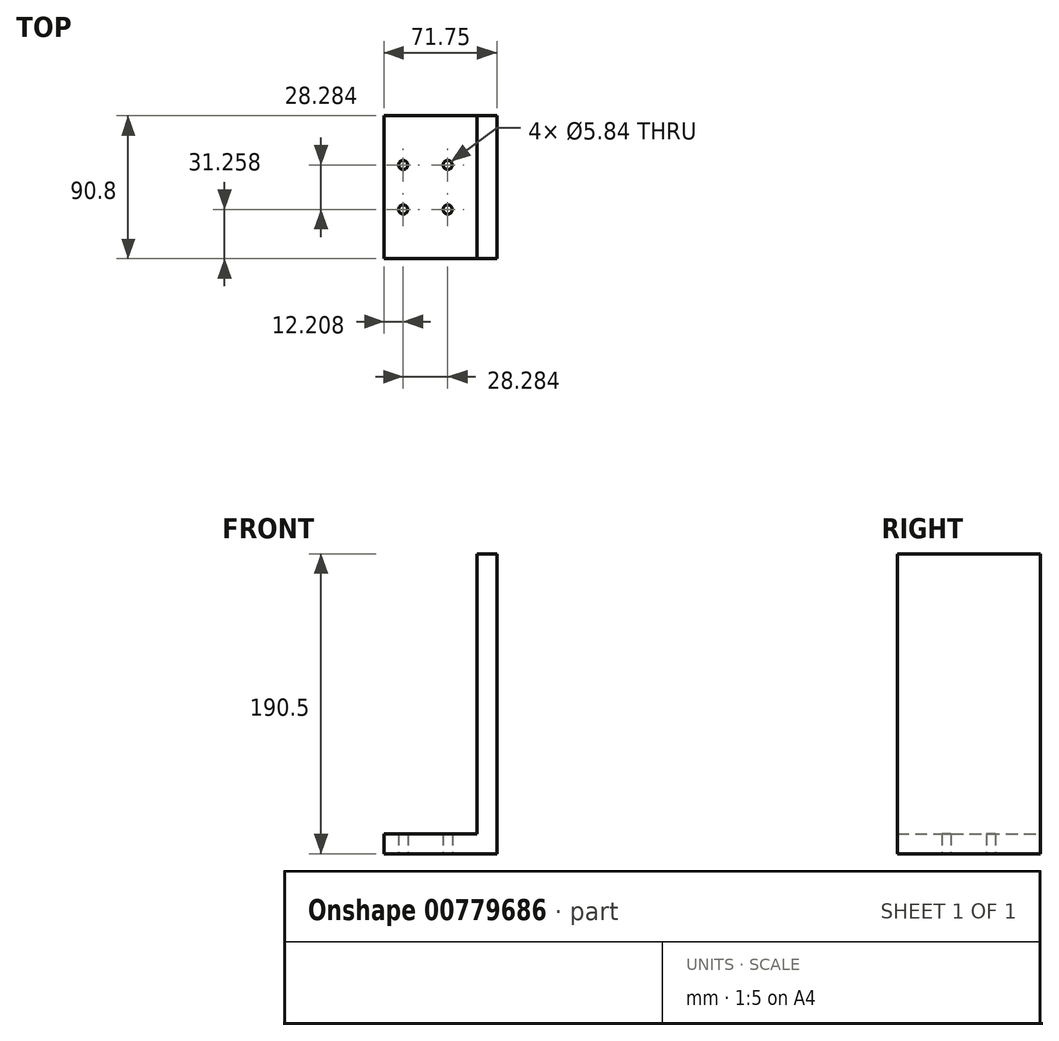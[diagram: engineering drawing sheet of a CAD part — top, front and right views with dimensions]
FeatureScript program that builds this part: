
annotation { "Feature Type Name" : "Feature", "Feature Type Description" : "" }
export const myFeature = defineFeature(function(context is Context, id is Id, definition is map)
    precondition{}
    {
        {
            var Q0;
            Q0=qCreatedBy(makeId("Top.planeOp"),FACE);
            var sketch = newSketch(context, id + "F0", { "sketchPlane" : qUnion([Q0])});
            skCircle(sketch, "E0", {"center": v(0, 0) * mm, "radius": 20 * mm, "construction": true});
            skLineSegment(sketch, "E1.bottom", {"start": v(20, 20) * mm, "end": v(-20, 20) * mm, "construction": true});
            skLineSegment(sketch, "E1.top", {"start": v(20, -20) * mm, "end": v(-20, -20) * mm, "construction": true});
            skLineSegment(sketch, "E1.left", {"start": v(20, 20) * mm, "end": v(20, -20) * mm, "construction": true});
            skLineSegment(sketch, "E1.right", {"start": v(-20, 20) * mm, "end": v(-20, -20) * mm, "construction": true});
            skLineSegment(sketch, "E2", {"start": v(-20, 20) * mm, "end": v(20, -20) * mm, "construction": true});
            skLineSegment(sketch, "E3", {"start": v(-20, -20) * mm, "end": v(20, 20) * mm, "construction": true});
            skCircle(sketch, "E4", {"center": v(-14.14, 14.14) * mm, "radius": 2.92 * mm});
            skCircle(sketch, "E5", {"center": v(14.14, 14.14) * mm, "radius": 2.92 * mm});
            skCircle(sketch, "E6", {"center": v(14.14, -14.14) * mm, "radius": 2.92 * mm});
            skCircle(sketch, "E7", {"center": v(-14.14, -14.14) * mm, "radius": 2.92 * mm});
            skLineSegment(sketch, "E8.bottom", {"start": v(-26.35, 45.4) * mm, "end": v(45.4, 45.4) * mm});
            skLineSegment(sketch, "E8.top", {"start": v(-26.35, -45.4) * mm, "end": v(45.4, -45.4) * mm});
            skLineSegment(sketch, "E8.left", {"start": v(-26.35, 45.4) * mm, "end": v(-26.35, -45.4) * mm});
            skLineSegment(sketch, "E8.right", {"start": v(45.4, 45.4) * mm, "end": v(45.4, -45.4) * mm});
            skLineSegment(sketch, "E9.bottom", {"start": v(45.4, 45.4) * mm, "end": v(32.7, 45.4) * mm});
            skLineSegment(sketch, "E9.top", {"start": v(45.4, -45.4) * mm, "end": v(32.7, -45.4) * mm});
            skLineSegment(sketch, "E9.right", {"start": v(32.7, 45.4) * mm, "end": v(32.7, -45.4) * mm});
            skSolve(sketch);
        }
        {
            var Q0;
            {var subQ0=sQuery(id+"F0.wireOp",EDGE,"E8.right");Q0=makeQuery(id+"F0.imprint","IMPRINT",FACE,{"disambiguationData":[TD([[makeQuery(id+"F0.imprint","IMPRINT",EDGE,{"derivedFrom":subQ0}),-1.0]])]});}
            var Q1;
            Q1=makeQuery(id+"F0.imprint","IMPRINT",FACE,{"disambiguationData":[TD([[makeQuery(id+"F0.imprint","IMPRINT",EDGE,{"derivedFrom":sQuery(id+"F0.wireOp",EDGE,"E4")}),-1.0]])]});
            extrude(context, id + "F1", {"entities" : qUnion([Q0, Q1]), "depth" : 12.7 * mm, "offsetDistance" : 25.4 * mm});
        }
        {
            var Q0;
            {var subQ0=sQuery(id+"F0.wireOp",EDGE,"E8.right");Q0=makeQuery(id+"F0.imprint","IMPRINT",FACE,{"disambiguationData":[TD([[makeQuery(id+"F0.imprint","IMPRINT",EDGE,{"derivedFrom":subQ0}),-1.0]])]});}
            extrude(context, id + "F2", {"entities" : qUnion([Q0]), "operationType" : NewBodyOperationType.ADD, "depth" : 190.5 * mm, "offsetDistance" : 25.4 * mm});
        }
        {
            var Q0;
            Q0=makeQuery(id+"F1.opExtrude","SWEPT_BODY",BODY,{"disambiguationData":[OSD([sQuery(id+"F0.wireOp",EDGE,"E4"),sQuery(id+"F0.wireOp",EDGE,"E5"),sQuery(id+"F0.wireOp",EDGE,"E6"),sQuery(id+"F0.wireOp",EDGE,"E7"),sQuery(id+"F0.wireOp",EDGE,"E8.bottom"),sQuery(id+"F0.wireOp",EDGE,"E8.top"),sQuery(id+"F0.wireOp",EDGE,"E8.left"),sQuery(id+"F0.wireOp",EDGE,"E8.right")])]});
            transform(context, id + "F3", {"entities" : qUnion([Q0]), "transformType" : TransformType.TRANSLATION_3D, "dx" : 0 * mm, "dy" : 0 * mm, "dz" : 0 * mm, "makeCopy" : true});
        }
        {
            var Q0;
            Q0=makeQuery(id+"F3.opPattern","COPY",BODY,{"derivedFrom":makeQuery(id+"F1.opExtrude","SWEPT_BODY",BODY,{"disambiguationData":[OSD([sQuery(id+"F0.wireOp",EDGE,"E4"),sQuery(id+"F0.wireOp",EDGE,"E5"),sQuery(id+"F0.wireOp",EDGE,"E6"),sQuery(id+"F0.wireOp",EDGE,"E7"),sQuery(id+"F0.wireOp",EDGE,"E8.bottom"),sQuery(id+"F0.wireOp",EDGE,"E8.top"),sQuery(id+"F0.wireOp",EDGE,"E8.left"),sQuery(id+"F0.wireOp",EDGE,"E8.right")])]}),"instanceName":"1"});
            deleteBodies(context, id + "F4", {"entities" : qUnion([Q0])});
        }
    });
